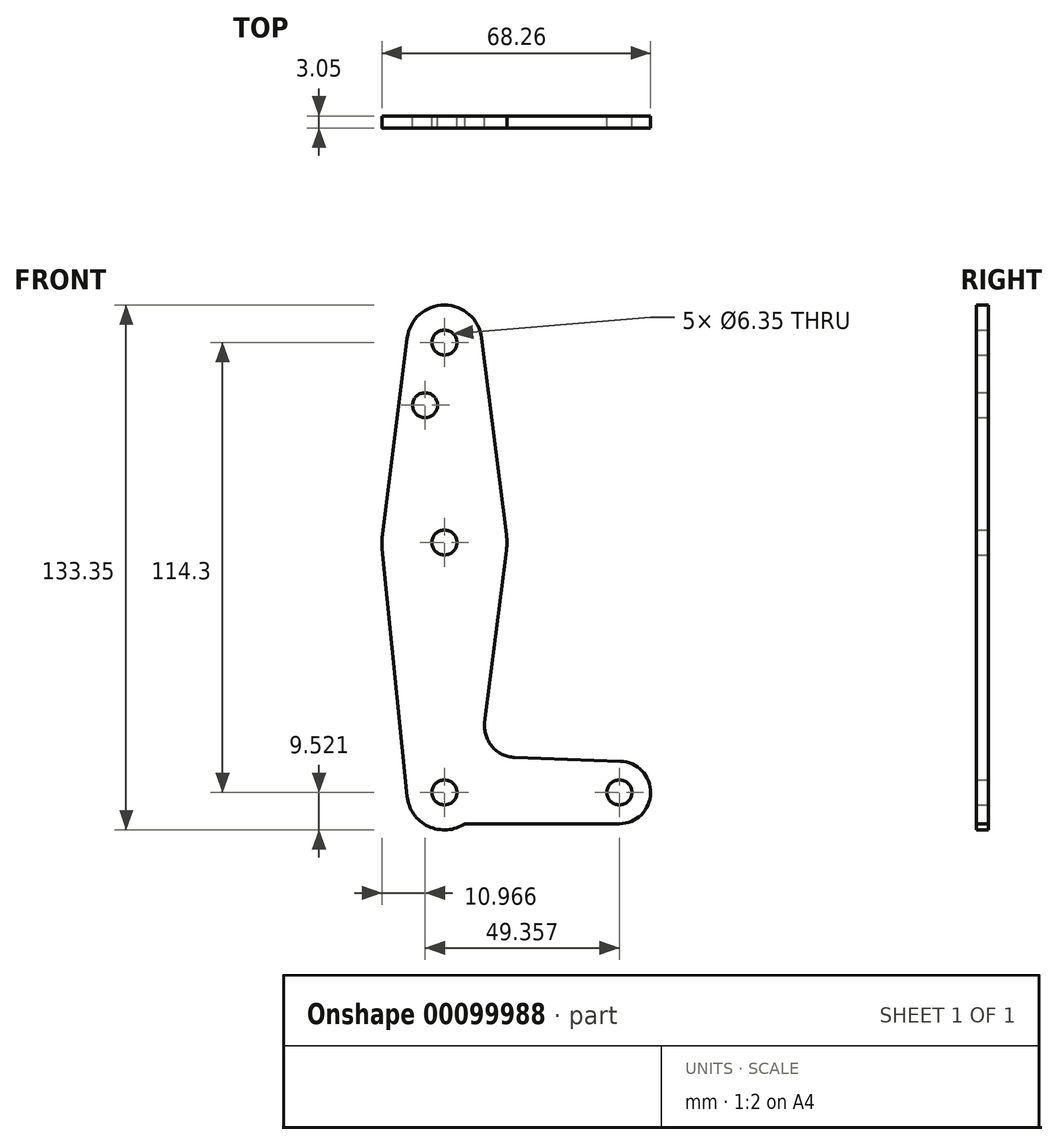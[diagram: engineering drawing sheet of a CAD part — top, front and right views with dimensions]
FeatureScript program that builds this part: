
annotation { "Feature Type Name" : "Feature", "Feature Type Description" : "" }
export const myFeature = defineFeature(function(context is Context, id is Id, definition is map)
    precondition{}
    {
        {
            var Q0;
            Q0=qCreatedBy(makeId("Front.planeOp"),FACE);
            var sketch = newSketch(context, id + "F0", { "sketchPlane" : qUnion([Q0])});
            skLineSegment(sketch, "E0", {"start": v(-40.08, 85.86) * mm, "end": v(-40.08, -28.44) * mm});
            skLineSegment(sketch, "E1", {"start": v(-40.08, -28.44) * mm, "end": v(4.37, -28.44) * mm});
            skCircle(sketch, "E2", {"center": v(-40.08, 85.86) * mm, "radius": 9.53 * mm});
            skCircle(sketch, "E3", {"center": v(-40.08, 35.06) * mm, "radius": 15.88 * mm});
            skCircle(sketch, "E4", {"center": v(-40.08, -28.44) * mm, "radius": 9.53 * mm});
            skCircle(sketch, "E5", {"center": v(4.37, -28.44) * mm, "radius": 7.94 * mm});
            skLineSegment(sketch, "E6", {"start": v(-49.53, 87.05) * mm, "end": v(-55.83, 37.04) * mm});
            skLineSegment(sketch, "E7", {"start": v(-30.63, 87.05) * mm, "end": v(-24.33, 37.04) * mm});
            skLineSegment(sketch, "E8", {"start": v(-55.87, 33.47) * mm, "end": v(-49.55, -29.4) * mm});
            skLineSegment(sketch, "E9", {"start": v(-24.33, 33.08) * mm, "end": v(-29.83, -10.6) * mm});
            skLineSegment(sketch, "E10", {"start": v(-22.23, -19.55) * mm, "end": v(4.66, -20.5) * mm});
            skLineSegment(sketch, "E11", {"start": v(-34.81, -36.38) * mm, "end": v(4.37, -36.38) * mm});
            skCircle(sketch, "E12", {"center": v(-40.08, 85.86) * mm, "radius": 3.18 * mm});
            skCircle(sketch, "E13", {"center": v(-40.08, 35.06) * mm, "radius": 3.18 * mm});
            skCircle(sketch, "E14", {"center": v(-40.08, -28.44) * mm, "radius": 3.18 * mm});
            skCircle(sketch, "E15", {"center": v(4.37, -28.44) * mm, "radius": 3.18 * mm});
            skCircle(sketch, "E16", {"center": v(-44.98, 69.93) * mm, "radius": 3.18 * mm});
            skArc(sketch, "E17.filletArc", {"start": v(-29.83, -10.6) * mm, "mid": v(-28, -16.75) * mm, "end": v(-22.23, -19.55) * mm});
            skSolve(sketch);
        }
        {
            var Q0;
            Q0 = qSketchRegion(id + "F0", true);
            var Q1;
            {var subQ0=sQuery(id+"F0.wireOp",EDGE,"E4");var subQ1=sQuery(id+"F0.wireOp",EDGE,"E0");var subQ2=makeQuery(id+"F0.imprint","INTERSECT",VERTEX,{"derivedFrom":[subQ1,subQ0]});Q1=makeQuery(id+"F0.imprint","IMPRINT",FACE,{"disambiguationData":[TD([[makeQuery(id+"F0.imprint","IMPRINT",EDGE,{"disambiguationData":[TD([[subQ2,-1.0]])],"derivedFrom":subQ1}),1.0]])]});}
            extrude(context, id + "F1", {"entities" : qUnion([Q0, Q1]), "depth" : 3.05 * mm});
        }
    });
